# Revit family: Niche_NobleCompany_306
name_source: partatom
category: Generic Models
revit_build: Autodesk Revit 2018 (Build: 20170223_1515(x64)
units: mm (PartAtom-declared; Revit-internal decimal feet)

## family parameters
Always vertical = Yes
Can host rebar = No
Cut with Voids When Loaded = No
Host = Wall
Part Type = Normal
Room Calculation Point = No
Round Connector Dimension = Use Diameter
Shared = No

## types (1)
- 306 Narrow Arch Combo
    Assembly Code = D2010700
    Depth = 0' - 4"
    Description = 306 Narrow Arch Combo Niche
    Height = 1' - 10 1/2"
    Installation-Fabrication = http://noblecompany.com
    Keynote = 10 28 00
    Manufacturer = Noble Company
    Manufacturer Fax = 231-799-8850
    Manufacturer Website = www.noblecompany.com
    Model = 306
    Niche Material = Acrylic Polymer Finish
    Product Data = http://www.arcat.com
    Product Properties = http://noblecompany.com
    Revision = R1_09-2016
    Sales Information = http://noblecompany.com
    Thickness = 0' - 1 1/8"
    URL = www.noblecompany.com
    Width = 0' - 8 1/4"

## geometry (parser evidence)
native form markers: Sweep x2
no freeform markers — native parametric forms only
